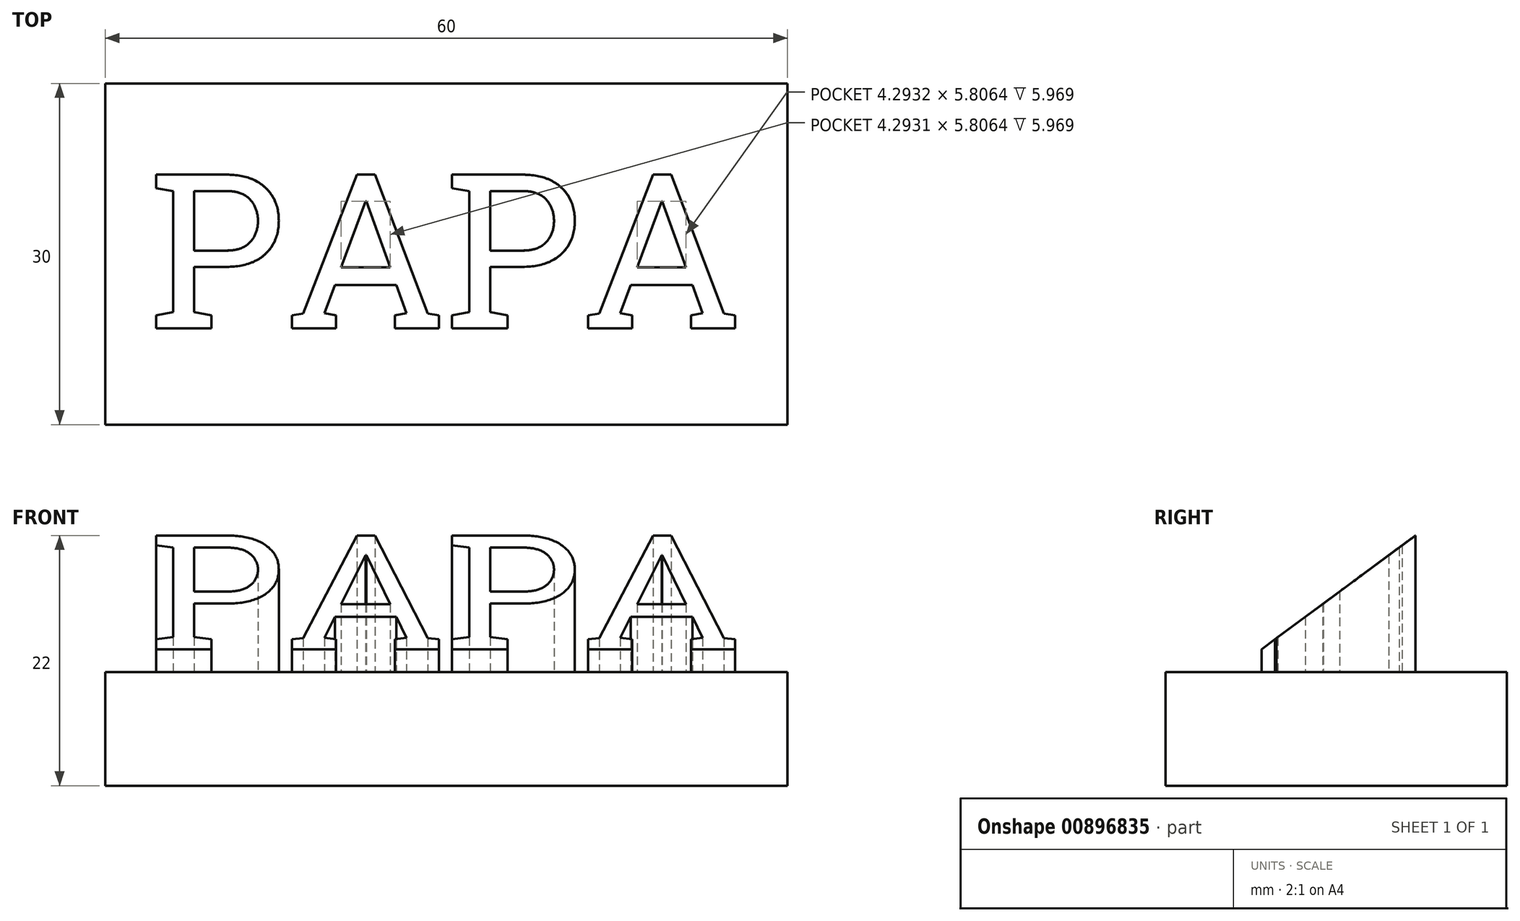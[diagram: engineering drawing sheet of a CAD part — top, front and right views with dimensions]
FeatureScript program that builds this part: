
annotation { "Feature Type Name" : "Feature", "Feature Type Description" : "" }
export const myFeature = defineFeature(function(context is Context, id is Id, definition is map)
    precondition{}
    {
        {
            var Q0;
            Q0=qCreatedBy(makeId("Top.planeOp"),FACE);
            var sketch = newSketch(context, id + "F0", { "sketchPlane" : qUnion([Q0])});
            skLineSegment(sketch, "E0.bottom", {"start": v(31.66, -15) * mm, "end": v(-28.34, -15) * mm});
            skLineSegment(sketch, "E0.top", {"start": v(31.66, 15) * mm, "end": v(-28.34, 15) * mm});
            skLineSegment(sketch, "E0.left", {"start": v(31.66, -15) * mm, "end": v(31.66, 15) * mm});
            skLineSegment(sketch, "E0.right", {"start": v(-28.34, -15) * mm, "end": v(-28.34, 15) * mm});
            skPoint(sketch, "E0.middle", {"position": v(1.66, 0) * mm});
            skSolve(sketch);
        }
        {
            var Q0;
            Q0=makeQuery(id+"F0.imprint","IMPRINT",FACE,{"disambiguationData":[TD([[makeQuery(id+"F0.imprint","IMPRINT",EDGE,{"derivedFrom":sQuery(id+"F0.wireOp",EDGE,"E0.bottom")}),-1.0]])]});
            extrude(context, id + "F1", {"entities" : qUnion([Q0]), "depth" : 10 * mm, "offsetDistance" : 25 * mm});
        }
        {
            var Q0;
            Q0=makeQuery(id+"F1.opExtrude","CAP_FACE",FACE,{"disambiguationData":[OSD([sQuery(id+"F0.wireOp",EDGE,"E0.bottom"),sQuery(id+"F0.wireOp",EDGE,"E0.top"),sQuery(id+"F0.wireOp",EDGE,"E0.left"),sQuery(id+"F0.wireOp",EDGE,"E0.right")])],"isStart":false});
            var sketch = newSketch(context, id + "F2", { "sketchPlane" : qUnion([Q0])});
            skLineSegment(sketch, "E1.0.0", {"start": v(31.66, -15) * mm, "end": v(31.66, 15) * mm});
            skLineSegment(sketch, "E1.0.1", {"start": v(31.66, 15) * mm, "end": v(-28.34, 15) * mm});
            skLineSegment(sketch, "E1.0.2", {"start": v(-28.34, 15) * mm, "end": v(-28.34, -15) * mm});
            skLineSegment(sketch, "E1.0.3", {"start": v(-28.34, -15) * mm, "end": v(31.66, -15) * mm});
            skLineSegment(sketch, "E2", {"start": v(-28.34, 12) * mm, "end": v(31.66, 12) * mm});
            skLineSegment(sketch, "E3", {"start": v(-28.34, -12) * mm, "end": v(31.66, -12) * mm});
            skPoint(sketch, "E3.startSnap0", {"position": v(-14.7, -12) * mm});
            skLineSegment(sketch, "E4", {"start": v(-26.34, -15) * mm, "end": v(-26.34, 15) * mm});
            skLineSegment(sketch, "E5", {"start": v(29.66, 15) * mm, "end": v(29.66, -15) * mm});
            skText(sketch, "E6", { "text": "PAPA", "fontName": "RobotoSlab-Regular.ttf"});
            const initialGuessF2  = {"E6": [-0.02452, -0.00655, 1, 0, 0.0137]};
            skSetInitialGuess(sketch, initialGuessF2);
            skSolve(sketch);
        }
        {
            var Q0;
            Q0=makeQuery(id+"F2.imprint","IMPRINT",FACE,{"disambiguationData":[TD([[makeQuery(id+"F2.imprint","IMPRINT",EDGE,{"derivedFrom":sQuery(id+"F2.wireOp",EDGE,"E6.sketch_text.stroke-0")}),-1.0]])]});
            var Q1;
            Q1=makeQuery(id+"F2.imprint","IMPRINT",FACE,{"disambiguationData":[TD([[makeQuery(id+"F2.imprint","IMPRINT",EDGE,{"derivedFrom":sQuery(id+"F2.wireOp",EDGE,"E6.sketch_text.stroke-23")}),-1.0]])]});
            var Q2;
            Q2=makeQuery(id+"F2.imprint","IMPRINT",FACE,{"disambiguationData":[TD([[makeQuery(id+"F2.imprint","IMPRINT",EDGE,{"derivedFrom":sQuery(id+"F2.wireOp",EDGE,"E6.sketch_text.stroke-43")}),-1.0]])]});
            var Q3;
            Q3=makeQuery(id+"F2.imprint","IMPRINT",FACE,{"disambiguationData":[TD([[makeQuery(id+"F2.imprint","IMPRINT",EDGE,{"derivedFrom":sQuery(id+"F2.wireOp",EDGE,"E6.sketch_text.stroke-66")}),-1.0]])]});
            extrude(context, id + "F3", {"entities" : qUnion([Q0, Q1, Q2, Q3]), "operationType" : NewBodyOperationType.ADD, "depth" : 12 * mm, "offsetDistance" : 25 * mm});
        }
        {
            var Q0;
            Q0=makeQuery(id+"F3.opExtrude","SWEPT_FACE",FACE,{"disambiguationData":[OSD([sQuery(id+"F2.wireOp",EDGE,"E6.sketch_text.stroke-9")])]});
            var sketch = newSketch(context, id + "F4", { "sketchPlane" : qUnion([Q0])});
            skLineSegment(sketch, "E7.0", {"start": v(6.55, 22) * mm, "end": v(6.55, 10) * mm});
            skLineSegment(sketch, "E8.0", {"start": v(-6.98, 22) * mm, "end": v(-6.98, 10) * mm});
            skLineSegment(sketch, "E9", {"start": v(6.55, 10) * mm, "end": v(6.55, 12) * mm});
            skLineSegment(sketch, "E10", {"start": v(6.55, 12) * mm, "end": v(-6.98, 22) * mm});
            skLineSegment(sketch, "E11", {"start": v(6.55, 22) * mm, "end": v(-6.98, 22) * mm});
            skSolve(sketch);
        }
        {
            var Q0;
            {var subQ0=sQuery(id+"F4.wireOp",EDGE,"E11");var subQ1=sQuery(id+"F4.wireOp",EDGE,"E10");var subQ2=makeQuery(id+"F4.imprint","INTERSECT",VERTEX,{"derivedFrom":[subQ1,subQ0]});Q0=makeQuery(id+"F4.imprint","IMPRINT",FACE,{"disambiguationData":[TD([[makeQuery(id+"F4.imprint","IMPRINT",EDGE,{"disambiguationData":[TD([[subQ2,1.0]])],"derivedFrom":subQ1}),-1.0]])]});}
            var Q1;
            {var subQ0=sQuery(id+"F4.wireOp",EDGE,"E11");var subQ1=sQuery(id+"F4.wireOp",EDGE,"E7.0");var subQ2=makeQuery(id+"F4.imprint","INTERSECT",VERTEX,{"derivedFrom":[subQ1,subQ0]});Q1=makeQuery(id+"F4.imprint","IMPRINT",FACE,{"disambiguationData":[TD([[makeQuery(id+"F4.imprint","IMPRINT",EDGE,{"disambiguationData":[TD([[subQ2,-1.0]])],"derivedFrom":subQ1}),-1.0]])]});}
            extrude(context, id + "F5", {"entities" : qUnion([Q0, Q1]), "operationType" : NewBodyOperationType.REMOVE, "oppositeDirection" : true, "depth" : 55 * mm, "offsetDistance" : 25 * mm});
        }
    });
